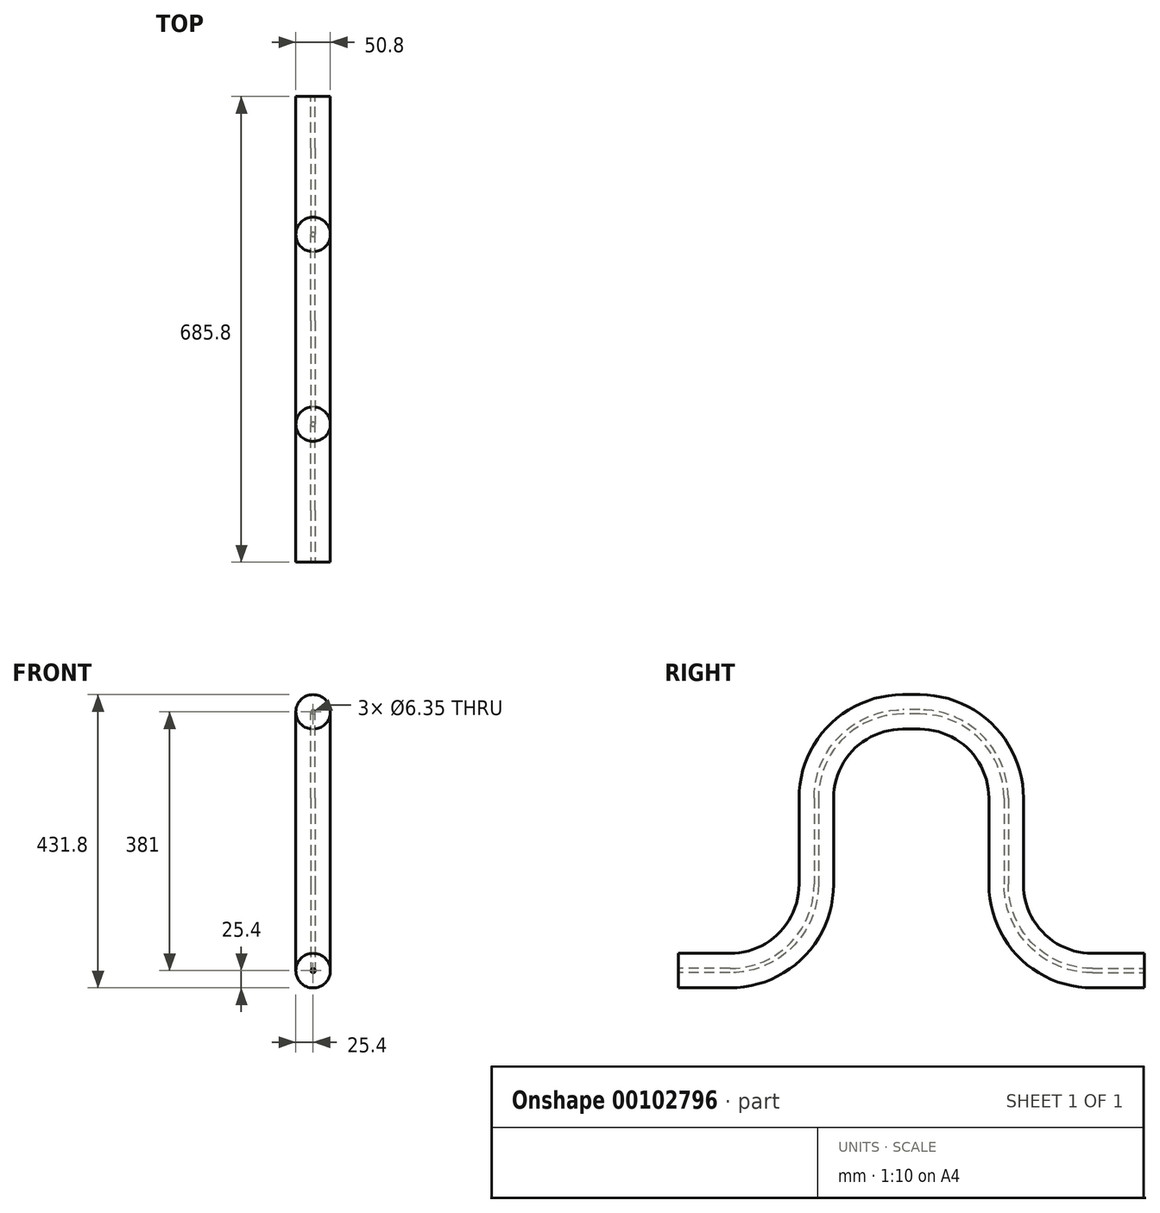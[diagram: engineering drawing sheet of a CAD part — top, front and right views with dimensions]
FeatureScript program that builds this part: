
annotation { "Feature Type Name" : "Feature", "Feature Type Description" : "" }
export const myFeature = defineFeature(function(context is Context, id is Id, definition is map)
    precondition{}
    {
        {
            var Q0;
            Q0=qCreatedBy(makeId("Front.planeOp"),FACE);
            var sketch = newSketch(context, id + "F0", { "sketchPlane" : qUnion([Q0])});
            skCircle(sketch, "E0", {"center": v(0, 0) * mm, "radius": 3.17 * mm});
            skCircle(sketch, "E1", {"center": v(0, 0) * mm, "radius": 25.4 * mm});
            skSolve(sketch);
        }
        {
            var Q0;
            Q0=qCreatedBy(makeId("Right.planeOp"),FACE);
            var sketch = newSketch(context, id + "F1", { "sketchPlane" : qUnion([Q0])});
            skLineSegment(sketch, "E2", {"start": v(0, 0) * mm, "end": v(-12.7, 0) * mm});
            skLineSegment(sketch, "E3", {"start": v(-139.7, -127) * mm, "end": v(-139.7, -254) * mm});
            skLineSegment(sketch, "E4", {"start": v(-266.7, -381) * mm, "end": v(-342.9, -381) * mm});
            skPoint(sketch, "E5.visualSharp", {"position": v(-139.7, 0) * mm});
            skArc(sketch, "E5.filletArc", {"start": v(-12.7, 0) * mm, "mid": v(-102.5, -37.2) * mm, "end": v(-139.7, -127) * mm});
            skPoint(sketch, "E6.visualSharp", {"position": v(-139.7, -381) * mm});
            skArc(sketch, "E6.filletArc", {"start": v(-266.7, -381) * mm, "mid": v(-176.9, -343.8) * mm, "end": v(-139.7, -254) * mm});
            skSolve(sketch);
        }
        {
            var Q0;
            Q0=makeQuery(id+"F0.imprint","IMPRINT",FACE,{"disambiguationData":[TD([[makeQuery(id+"F0.imprint","IMPRINT",EDGE,{"derivedFrom":sQuery(id+"F0.wireOp",EDGE,"E0")}),-1.0]])]});
            var Q1;
            Q1=sQuery(id+"F1.wireOp",EDGE,"E2");
            var Q2;
            Q2=sQuery(id+"F1.wireOp",EDGE,"E5.filletArc");
            var Q3;
            Q3=sQuery(id+"F1.wireOp",EDGE,"E3");
            var Q4;
            Q4=sQuery(id+"F1.wireOp",EDGE,"E6.filletArc");
            var Q5;
            Q5=sQuery(id+"F1.wireOp",EDGE,"E4");
            sweep(context, id + "F2", {"profiles" : qUnion([Q0]), "path" : qUnion([Q1, Q2, Q3, Q4, Q5])});
        }
        {
            var Q0;
            Q0=makeQuery(id+"F2.opSweep","SWEPT_BODY",BODY,{"disambiguationData":[OSD([sQuery(id+"F0.wireOp",EDGE,"E0"),sQuery(id+"F0.wireOp",EDGE,"E1"),sQuery(id+"F1.wireOp",EDGE,"E4")])]});
            var Q1;
            Q1=makeQuery(id+"F2.opSweep","CAP_FACE",FACE,{"disambiguationData":[OSD([sQuery(id+"F0.wireOp",EDGE,"E0"),sQuery(id+"F0.wireOp",EDGE,"E1"),sQuery(id+"F1.wireOp",VERTEX,"E2.start")])],"isStart":true});
            mirror(context, id + "F3", {"operationType" : NewBodyOperationType.ADD, "entities" : qUnion([Q0]), "mirrorPlane" : qUnion([Q1])});
        }
    });
